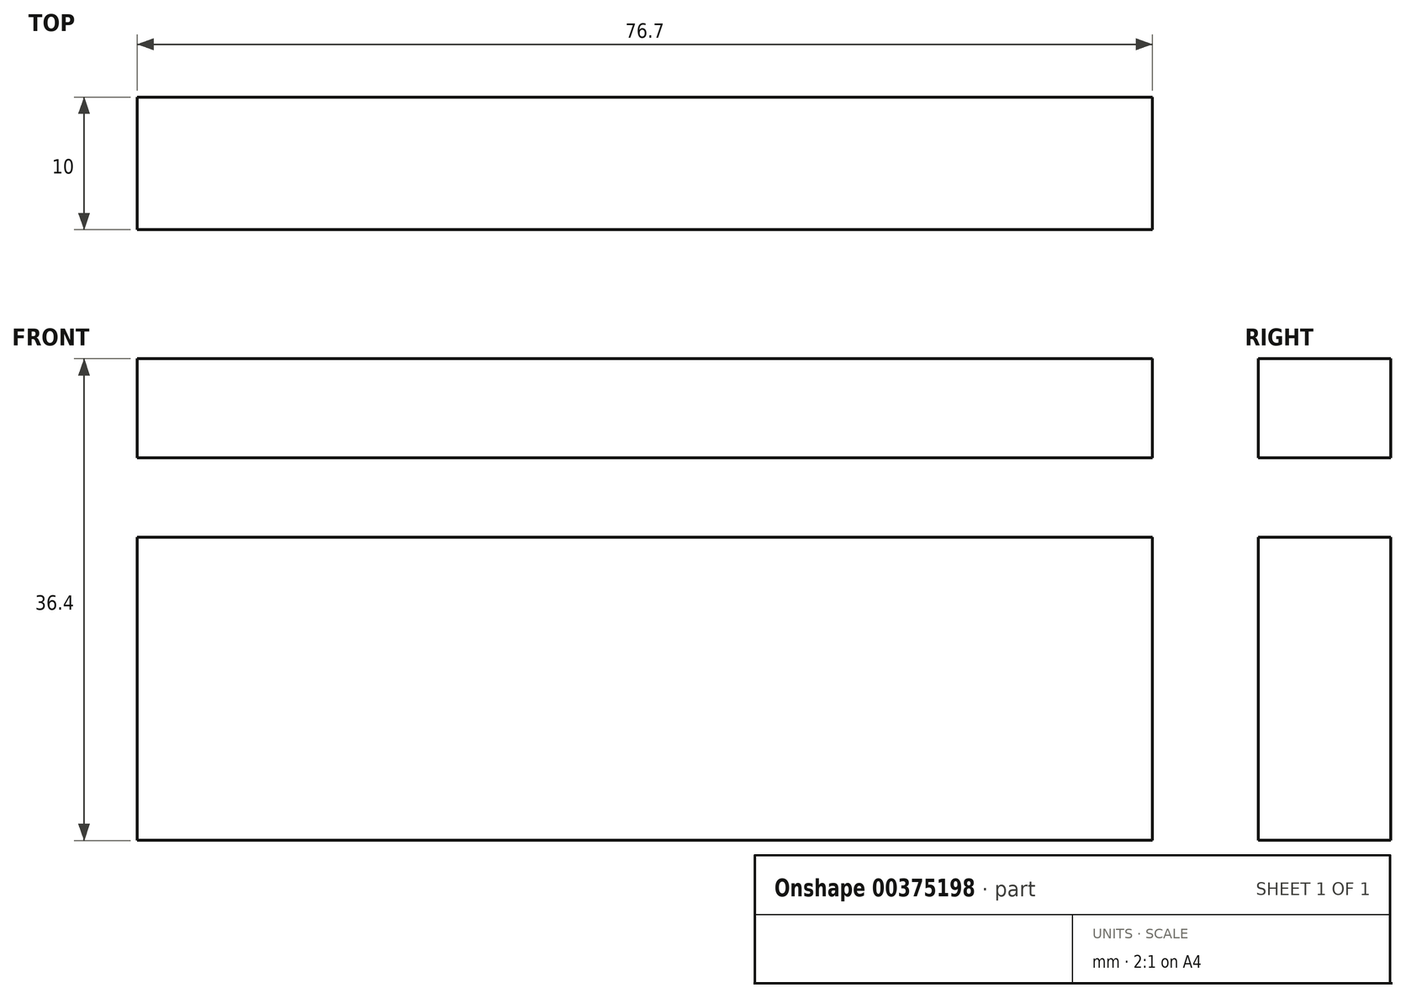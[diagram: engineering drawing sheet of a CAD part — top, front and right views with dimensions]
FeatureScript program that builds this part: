
annotation { "Feature Type Name" : "Feature", "Feature Type Description" : "" }
export const myFeature = defineFeature(function(context is Context, id is Id, definition is map)
    precondition{}
    {
        {
            var Q0;
            Q0=qCreatedBy(makeId("Front.planeOp"),FACE);
            var sketch = newSketch(context, id + "F0", { "sketchPlane" : qUnion([Q0])});
            skLineSegment(sketch, "E0.bottom", {"start": v(-46.62, 26.77) * mm, "end": v(30.08, 26.77) * mm});
            skLineSegment(sketch, "E0.top", {"start": v(-46.62, -9.63) * mm, "end": v(30.08, -9.63) * mm});
            skLineSegment(sketch, "E0.left", {"start": v(-46.62, 26.77) * mm, "end": v(-46.62, -9.63) * mm});
            skLineSegment(sketch, "E0.right", {"start": v(30.08, 26.77) * mm, "end": v(30.08, -9.63) * mm});
            skSolve(sketch);
        }
        {
            var Q0;
            Q0=makeQuery(id+"F0.imprint","IMPRINT",FACE,{"disambiguationData":[TD([[makeQuery(id+"F0.imprint","IMPRINT",EDGE,{"derivedFrom":sQuery(id+"F0.wireOp",EDGE,"E0.bottom")}),-1.0]])]});
            extrude(context, id + "F1", {"entities" : qUnion([Q0]), "depth" : 10 * mm});
        }
        {
            var Q0;
            Q0=makeQuery(id+"F1.opExtrude","SWEPT_FACE",FACE,{"disambiguationData":[OSD([sQuery(id+"F0.wireOp",EDGE,"E0.right")])]});
            var sketch = newSketch(context, id + "F2", { "sketchPlane" : qUnion([Q0])});
            skLineSegment(sketch, "E1.bottom", {"start": v(-10, 19.3) * mm, "end": v(0, 19.3) * mm});
            skLineSegment(sketch, "E1.top", {"start": v(-10, 13.28) * mm, "end": v(0, 13.28) * mm});
            skLineSegment(sketch, "E1.left", {"start": v(-10, 19.3) * mm, "end": v(-10, 13.28) * mm});
            skLineSegment(sketch, "E1.right", {"start": v(0, 19.3) * mm, "end": v(0, 13.28) * mm});
            skLineSegment(sketch, "E2.bottom", {"start": v(-10, 2.73) * mm, "end": v(0, 2.73) * mm});
            skLineSegment(sketch, "E2.top", {"start": v(-10, -3.63) * mm, "end": v(0, -3.63) * mm});
            skLineSegment(sketch, "E2.left", {"start": v(-10, 2.73) * mm, "end": v(-10, -3.63) * mm});
            skLineSegment(sketch, "E2.right", {"start": v(0, 2.73) * mm, "end": v(0, -3.63) * mm});
            skSolve(sketch);
        }
        {
            var Q0;
            Q0=makeQuery(id+"F2.imprint","IMPRINT",FACE,{"disambiguationData":[TD([[makeQuery(id+"F2.imprint","IMPRINT",EDGE,{"derivedFrom":sQuery(id+"F2.wireOp",EDGE,"E1.bottom")}),-1.0]])]});
            extrude(context, id + "F3", {"entities" : qUnion([Q0]), "operationType" : NewBodyOperationType.REMOVE, "endBound" : BoundingType.UP_TO_NEXT, "oppositeDirection" : true, "depth" : 10 * mm, "hasSecondDirection" : true, "secondDirectionOppositeDirection" : false, "secondDirectionDepth" : 25.4 * mm});
        }
    });
